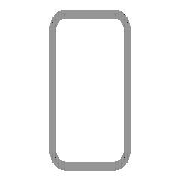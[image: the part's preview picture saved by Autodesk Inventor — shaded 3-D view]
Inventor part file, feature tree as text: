
AUTODESK INVENTOR PART (.ipt)
format: ipt  version: 2025 (Build 290162010, 162A)  size: 156,672 bytes
history: native  units: mm (DEFAULTED — no unit token found)
features: other x3, sketch x2, extrude x1, plane x1
ambient origin geometry x8: Origin, YZ Plane, XZ Plane, XY Plane, X Axis, Y Axis, Z Axis, Center Point
bodies: Solid1 (feature_tree), Body (feature_tree)
feature tree (7):
  other  "Driven Length"
  other  "Start plane"
  other  "End plane"
  extrude  "Extrusion3"  TaperAngle=0.0deg  [1 undecoded]
  sketch  "Sketch3"  dims[d3=350.0mm d4=0.0mm]
  plane  "Work Plane3"
  sketch  "Sketch6"  dims[d7=4.5mm d10=80.0mm d11=40.0mm d12=3.0mm d13=-0.0mm d14=350.0mm d15=40.0mm d16=20.0mm d17=90.0deg d18=350.0mm d22=8.028515mm d23=8.028515mm d24=0.0mm d25=0.0mm]
note: 1 required parameter value undecoded (feature->parameter linkage not recoverable at this tier; creation-order binding heuristic only, values carry confidence <= 0.55)
